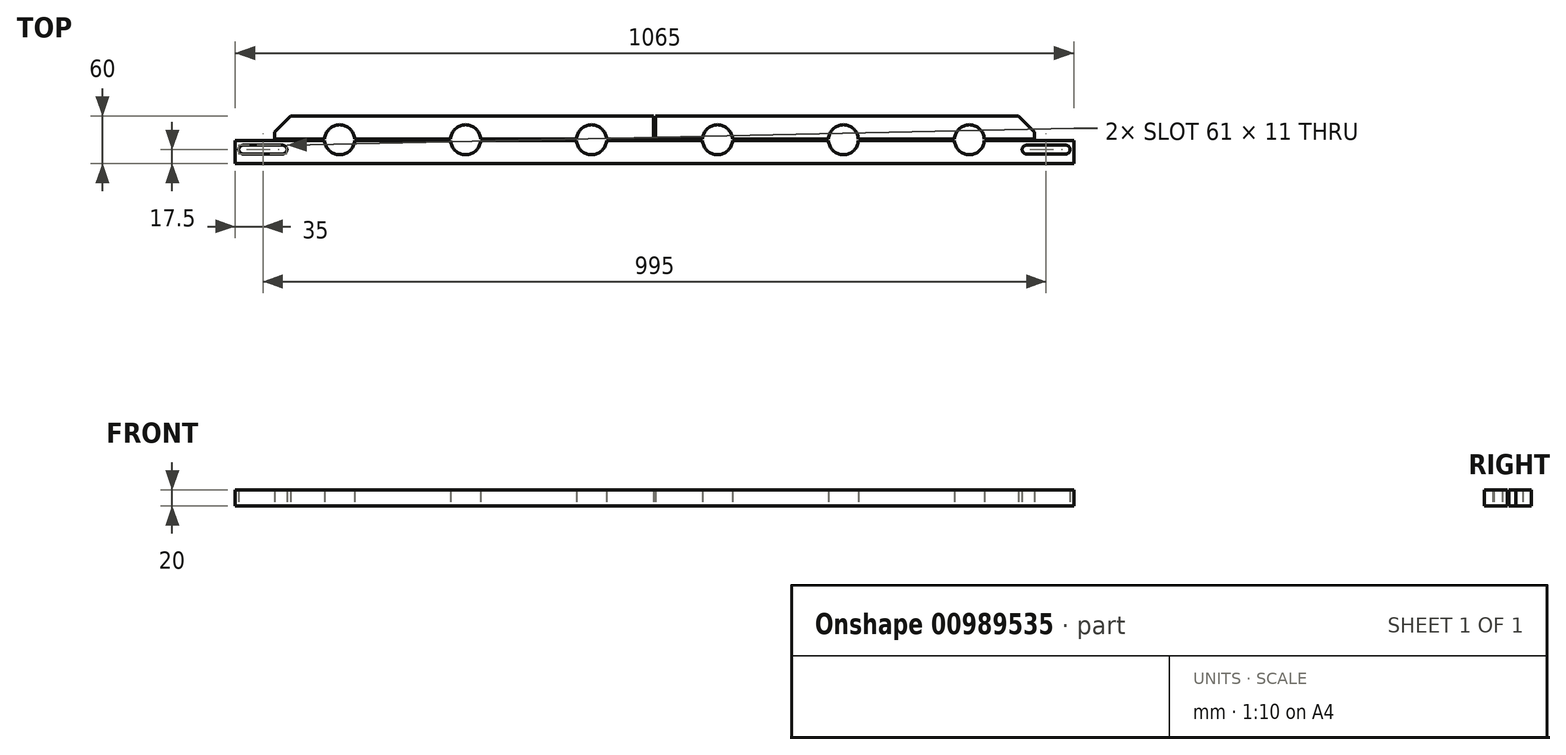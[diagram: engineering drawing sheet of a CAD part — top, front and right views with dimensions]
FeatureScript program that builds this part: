
annotation { "Feature Type Name" : "Feature", "Feature Type Description" : "" }
export const myFeature = defineFeature(function(context is Context, id is Id, definition is map)
    precondition{}
    {
        {
            var Q0;
            Q0=qCreatedBy(makeId("Top.planeOp"),FACE);
            var sketch = newSketch(context, id + "F0", { "sketchPlane" : qUnion([Q0])});
            skLineSegment(sketch, "E0.bottom", {"start": v(462.5, 30) * mm, "end": v(1, 30) * mm});
            skLineSegment(sketch, "E0.top", {"start": v(532.5, -30) * mm, "end": v(-532.5, -30) * mm});
            skLineSegment(sketch, "E0.left", {"start": v(532.5, -1) * mm, "end": v(532.5, -30) * mm});
            skLineSegment(sketch, "E0.right", {"start": v(-532.5, -1) * mm, "end": v(-532.5, -30) * mm});
            skPoint(sketch, "E0.middle", {"position": v(0, 0) * mm});
            skLineSegment(sketch, "E1", {"start": v(0, 190.2) * mm, "end": v(0, -272.36) * mm, "construction": true});
            skPoint(sketch, "E1.endSnap0", {"position": v(0, -30) * mm});
            skLineSegment(sketch, "E2", {"start": v(-80, 190.2) * mm, "end": v(-80, -272.36) * mm, "construction": true});
            skLineSegment(sketch, "E3", {"start": v(-240, 190.2) * mm, "end": v(-240, -272.36) * mm, "construction": true});
            skLineSegment(sketch, "E4", {"start": v(-400, 190.2) * mm, "end": v(-400, -272.36) * mm, "construction": true});
            skLineSegment(sketch, "E5", {"start": v(80, 190.2) * mm, "end": v(80, -272.36) * mm, "construction": true});
            skLineSegment(sketch, "E6", {"start": v(240, 190.2) * mm, "end": v(240, -272.36) * mm, "construction": true});
            skLineSegment(sketch, "E7", {"start": v(400, 190.2) * mm, "end": v(400, -272.36) * mm, "construction": true});
            skLineSegment(sketch, "E8", {"start": v(-573.3, -12.5) * mm, "end": v(-411.4, -12.5) * mm, "construction": true});
            skLineSegment(sketch, "E9", {"start": v(408.06, -12.5) * mm, "end": v(612.05, -12.5) * mm, "construction": true});
            skArc(sketch, "E10", {"start": v(522.5, -18) * mm, "mid": v(528, -12.5) * mm, "end": v(522.5, -7) * mm});
            skArc(sketch, "E11", {"start": v(472.5, -7) * mm, "mid": v(467, -12.5) * mm, "end": v(472.5, -18) * mm});
            skLineSegment(sketch, "E12", {"start": v(472.5, -7) * mm, "end": v(522.5, -7) * mm});
            skLineSegment(sketch, "E13", {"start": v(472.5, -18) * mm, "end": v(522.5, -18) * mm});
            skArc(sketch, "E14", {"start": v(-522.5, -7) * mm, "mid": v(-528, -12.5) * mm, "end": v(-522.5, -18) * mm});
            skArc(sketch, "E15", {"start": v(-472.5, -18) * mm, "mid": v(-467, -12.5) * mm, "end": v(-472.5, -7) * mm});
            skLineSegment(sketch, "E16", {"start": v(-522.5, -7) * mm, "end": v(-472.5, -7) * mm});
            skLineSegment(sketch, "E17", {"start": v(-522.5, -18) * mm, "end": v(-472.5, -18) * mm});
            skArc(sketch, "E18", {"start": v(-418.97, -1) * mm, "mid": v(-400, -19) * mm, "end": v(-381.03, -1) * mm});
            skArc(sketch, "E19", {"start": v(-258.97, -1) * mm, "mid": v(-240, -19) * mm, "end": v(-221.03, -1) * mm});
            skArc(sketch, "E20", {"start": v(-98.97, -1) * mm, "mid": v(-80, -19) * mm, "end": v(-61.03, -1) * mm});
            skArc(sketch, "E21", {"start": v(61.03, -1) * mm, "mid": v(80, -19) * mm, "end": v(98.97, -1) * mm});
            skArc(sketch, "E22", {"start": v(221.03, -1) * mm, "mid": v(240, -19) * mm, "end": v(258.97, -1) * mm});
            skArc(sketch, "E23", {"start": v(381.03, -1) * mm, "mid": v(400, -19) * mm, "end": v(418.97, -1) * mm});
            skLineSegment(sketch, "E24", {"start": v(1, 30) * mm, "end": v(1, 1) * mm});
            skLineSegment(sketch, "E25", {"start": v(-1, 1) * mm, "end": v(-1, 30) * mm});
            skLineSegment(sketch, "E26", {"start": v(-482.5, 1) * mm, "end": v(-418.97, 1) * mm});
            skLineSegment(sketch, "E27", {"start": v(532.5, -1) * mm, "end": v(418.97, -1) * mm});
            skLineSegment(sketch, "E28", {"start": v(-482.5, 10) * mm, "end": v(-462.5, 30) * mm});
            skLineSegment(sketch, "E29", {"start": v(-482.5, 10) * mm, "end": v(-482.5, 1) * mm});
            skPoint(sketch, "E30.orphan", {"position": v(-532.5, 30) * mm});
            skLineSegment(sketch, "E31", {"start": v(482.5, 1) * mm, "end": v(482.5, 10) * mm});
            skLineSegment(sketch, "E32", {"start": v(482.5, 10) * mm, "end": v(462.5, 30) * mm});
            skPoint(sketch, "E33.orphan", {"position": v(532.5, 30) * mm});
            skArc(sketch, "E34.trimOffspring", {"start": v(-381.03, 1) * mm, "mid": v(-400, 19) * mm, "end": v(-418.97, 1) * mm});
            skLineSegment(sketch, "E35.trimOffspring", {"start": v(-381.03, 1) * mm, "end": v(-258.97, 1) * mm});
            skLineSegment(sketch, "E36.trimOffspring", {"start": v(-418.97, -1) * mm, "end": v(-532.5, -1) * mm});
            skLineSegment(sketch, "E37.trimOffspring", {"start": v(-221.03, 1) * mm, "end": v(-98.97, 1) * mm});
            skLineSegment(sketch, "E38.trimOffspring", {"start": v(-258.97, -1) * mm, "end": v(-381.03, -1) * mm});
            skArc(sketch, "E39.trimOffspring", {"start": v(-221.03, 1) * mm, "mid": v(-240, 19) * mm, "end": v(-258.97, 1) * mm});
            skLineSegment(sketch, "E40.trimOffspring", {"start": v(-61.03, 1) * mm, "end": v(-1, 1) * mm});
            skLineSegment(sketch, "E41.trimOffspring", {"start": v(-98.97, -1) * mm, "end": v(-221.03, -1) * mm});
            skArc(sketch, "E42.trimOffspring", {"start": v(-61.03, 1) * mm, "mid": v(-80, 19) * mm, "end": v(-98.97, 1) * mm});
            skLineSegment(sketch, "E43.trimOffspring", {"start": v(1, 0) * mm, "end": v(701.61, 0) * mm, "construction": true});
            skLineSegment(sketch, "E44.trimOffspring", {"start": v(1, 1) * mm, "end": v(61.03, 1) * mm});
            skLineSegment(sketch, "E45.trimOffspring", {"start": v(-1, 30) * mm, "end": v(-462.5, 30) * mm});
            skLineSegment(sketch, "E46.trimOffspring", {"start": v(98.97, 1) * mm, "end": v(221.03, 1) * mm});
            skLineSegment(sketch, "E47.trimOffspring", {"start": v(61.03, -1) * mm, "end": v(-61.03, -1) * mm});
            skArc(sketch, "E48.trimOffspring", {"start": v(98.97, 1) * mm, "mid": v(80, 19) * mm, "end": v(61.03, 1) * mm});
            skLineSegment(sketch, "E49.trimOffspring", {"start": v(221.03, -1) * mm, "end": v(98.97, -1) * mm});
            skLineSegment(sketch, "E50.trimOffspring", {"start": v(258.97, 1) * mm, "end": v(381.03, 1) * mm});
            skArc(sketch, "E51.trimOffspring", {"start": v(258.97, 1) * mm, "mid": v(240, 19) * mm, "end": v(221.03, 1) * mm});
            skLineSegment(sketch, "E52.trimOffspring", {"start": v(418.97, 1) * mm, "end": v(482.5, 1) * mm});
            skArc(sketch, "E53.trimOffspring", {"start": v(418.97, 1) * mm, "mid": v(400, 19) * mm, "end": v(381.03, 1) * mm});
            skLineSegment(sketch, "E54.trimOffspring", {"start": v(381.03, -1) * mm, "end": v(258.97, -1) * mm});
            skPoint(sketch, "E55.end.orphan", {"position": v(-532.5, 0) * mm});
            skPoint(sketch, "E56.orphan", {"position": v(-532.5, 1) * mm});
            skSolve(sketch);
        }
        {
            var Q0;
            Q0 = qSketchRegion(id + "F0", true);
            extrude(context, id + "F1", {"entities" : qUnion([Q0]), "depth" : 20 * mm, "offsetDistance" : 25 * mm});
        }
    });
